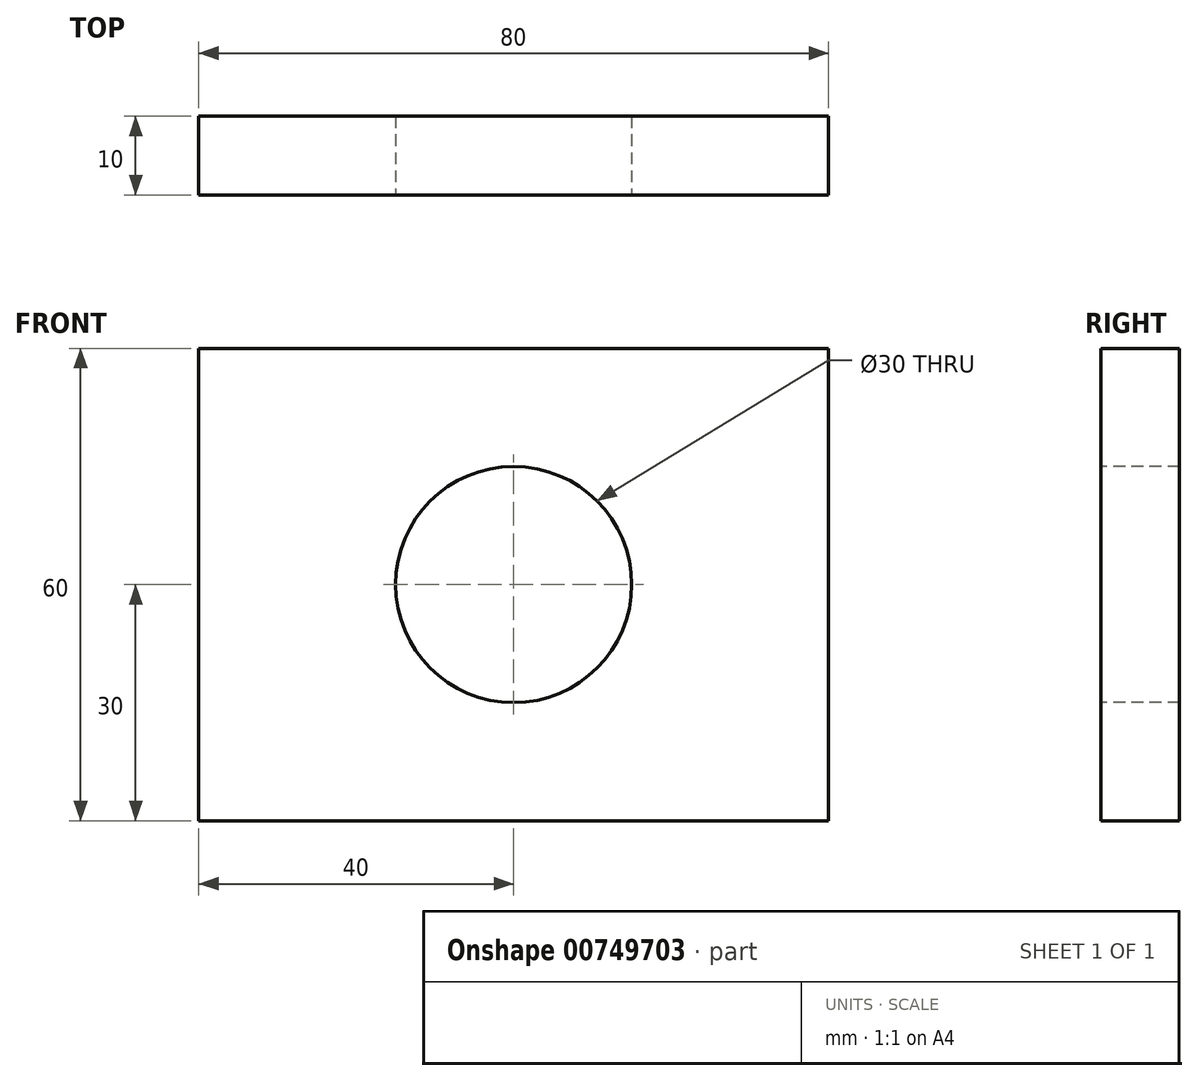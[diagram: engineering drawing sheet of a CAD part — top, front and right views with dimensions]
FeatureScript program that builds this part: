
annotation { "Feature Type Name" : "Feature", "Feature Type Description" : "" }
export const myFeature = defineFeature(function(context is Context, id is Id, definition is map)
    precondition{}
    {
        {
            var Q0;
            Q0=qCreatedBy(makeId("Front.planeOp"),FACE);
            var sketch = newSketch(context, id + "F0", { "sketchPlane" : qUnion([Q0])});
            skLineSegment(sketch, "E0.bottom", {"start": v(0, 0) * mm, "end": v(-80, 0) * mm});
            skLineSegment(sketch, "E0.top", {"start": v(0, 60) * mm, "end": v(-80, 60) * mm});
            skLineSegment(sketch, "E0.left", {"start": v(0, 0) * mm, "end": v(0, 60) * mm});
            skLineSegment(sketch, "E0.right", {"start": v(-80, 0) * mm, "end": v(-80, 60) * mm});
            skLineSegment(sketch, "E1", {"start": v(-40, 60) * mm, "end": v(-40, 0) * mm});
            skPoint(sketch, "E2.end.orphan", {"position": v(0, 30) * mm});
            skPoint(sketch, "E2.start.orphan", {"position": v(-40, 30) * mm});
            skLineSegment(sketch, "E3", {"start": v(-80, 30) * mm, "end": v(0, 30) * mm});
            skSolve(sketch);
        }
        {
            var Q0;
            Q0 = qSketchRegion(id + "F0", true);
            extrude(context, id + "F1", {"entities" : qUnion([Q0]), "depth" : 10 * mm, "offsetDistance" : 25 * mm});
        }
        {
            var Q0;
            Q0=makeQuery(id+"F1.opExtrude","CAP_FACE",FACE,{"disambiguationData":[OSD([sQuery(id+"F0.wireOp",EDGE,"E0.bottom"),sQuery(id+"F0.wireOp",EDGE,"E0.top"),sQuery(id+"F0.wireOp",EDGE,"E0.left"),sQuery(id+"F0.wireOp",EDGE,"E0.right")])],"isStart":false});
            var sketch = newSketch(context, id + "F2", { "sketchPlane" : qUnion([Q0])});
            skCircle(sketch, "E4", {"center": v(-40, 30) * mm, "radius": 15 * mm});
            skPoint(sketch, "E4.centerSnap0", {"position": v(-40, 0) * mm});
            skPoint(sketch, "E4.centerSnap1", {"position": v(0, 30) * mm});
            skSolve(sketch);
        }
        {
            var Q0;
            Q0 = qSketchRegion(id + "F2", true);
            extrude(context, id + "F3", {"entities" : qUnion([Q0]), "operationType" : NewBodyOperationType.REMOVE, "endBound" : BoundingType.THROUGH_ALL, "oppositeDirection" : true, "depth" : 25 * mm, "offsetDistance" : 25 * mm});
        }
    });
